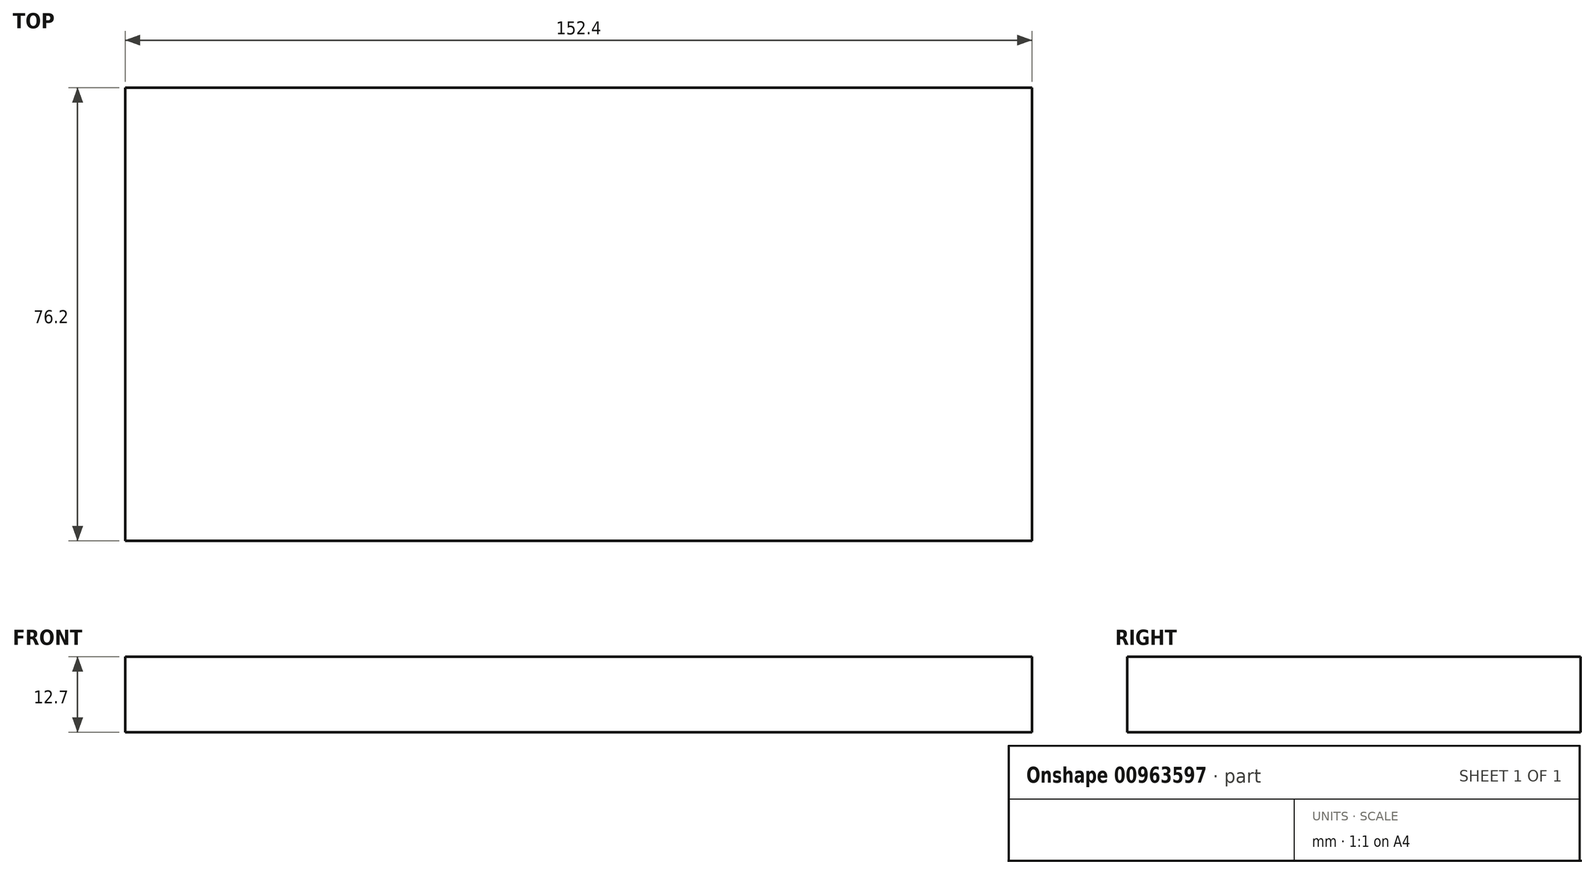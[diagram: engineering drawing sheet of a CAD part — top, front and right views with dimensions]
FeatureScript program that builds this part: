
annotation { "Feature Type Name" : "Feature", "Feature Type Description" : "" }
export const myFeature = defineFeature(function(context is Context, id is Id, definition is map)
    precondition{}
    {
        {
            var Q0;
            Q0=qCreatedBy(makeId("Top.planeOp"),FACE);
            var sketch = newSketch(context, id + "F0", { "sketchPlane" : qUnion([Q0])});
            skLineSegment(sketch, "E0.bottom", {"start": v(-76.2, 38.1) * mm, "end": v(76.2, 38.1) * mm});
            skLineSegment(sketch, "E0.top", {"start": v(-76.2, -38.1) * mm, "end": v(76.2, -38.1) * mm});
            skLineSegment(sketch, "E0.left", {"start": v(-76.2, 38.1) * mm, "end": v(-76.2, -38.1) * mm});
            skLineSegment(sketch, "E0.right", {"start": v(76.2, 38.1) * mm, "end": v(76.2, -38.1) * mm});
            skPoint(sketch, "E0.middle", {"position": v(0, 0) * mm});
            skSolve(sketch);
        }
        {
            var Q0;
            Q0 = qSketchRegion(id + "F0", true);
            extrude(context, id + "F1", {"entities" : qUnion([Q0]), "depth" : 12.7 * mm, "offsetDistance" : 25.4 * mm});
        }
    });
